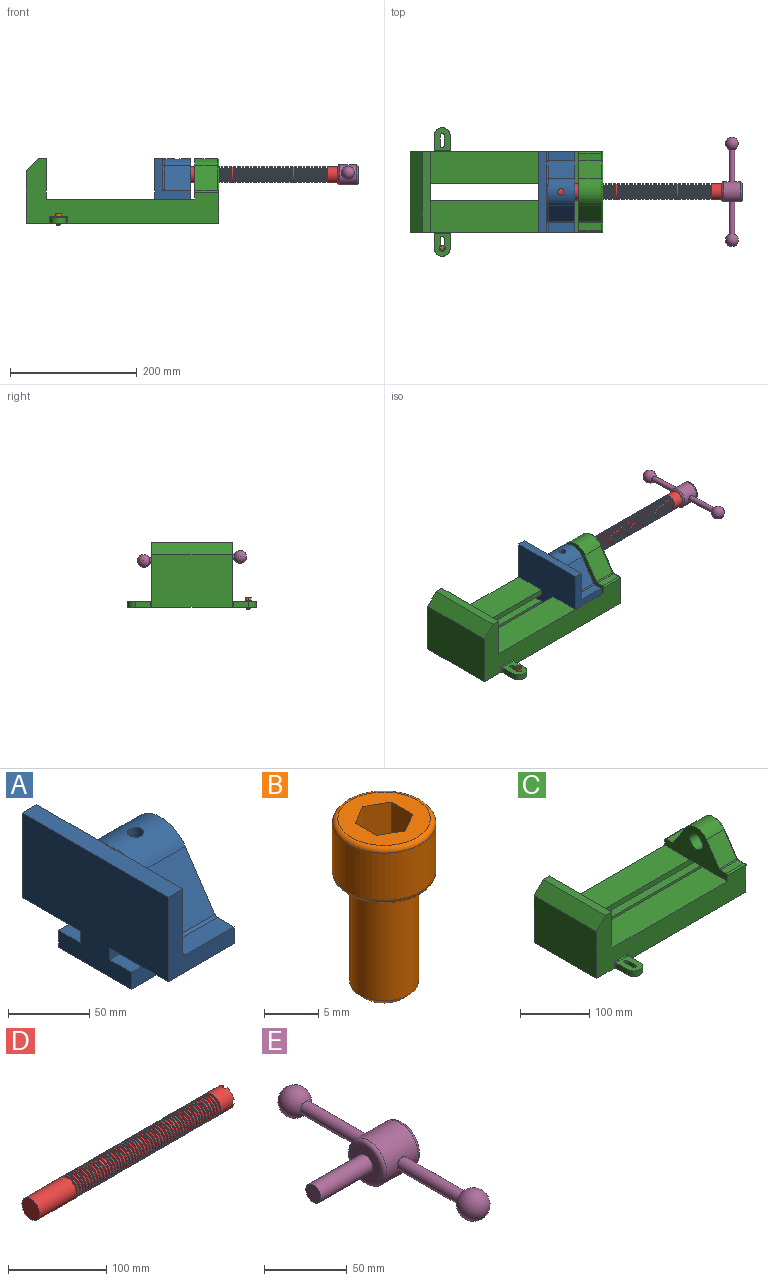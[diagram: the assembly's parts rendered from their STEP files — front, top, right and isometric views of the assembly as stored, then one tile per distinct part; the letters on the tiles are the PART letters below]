
ASSEMBLY  parts=5 mates=5
PART A: 36 faces, bbox 57.2x127x89 mm
  f0: plane 57.15x50.8mm, normal (0,0,-1), area 2903.2mm2, adj f6,f9,f10,f23
  f1: cylinder r=12.7mm len=44.45mm, axis (1,0,0), area 3464.3mm2, adj f6,f15,f16
  f2: plane 41.91x14.52mm, normal (0,0,1), area 608.5mm2, adj f6,f11,f24,f25
  f3: plane 51.86x48.26mm, normal (1,0,0), area 1495.7mm2, adj f8,f10,f31,f33,f35
  f4: plane 51.86x48.26mm, normal (1,0,0), area 1495.7mm2, adj f8,f11,f24,f28,f29
  f5: plane 57.15x50.8mm, normal (0,0,-1), area 2903.2mm2, adj f6,f9,f11,f22
  f6: plane 127x85.09mm, normal (1,0,0), area 5190.6mm2, adj f0,f1,f2,f5,f7,f10,f11,f12
  f7: plane 41.91x14.52mm, normal (0,0,1), area 608.5mm2, adj f6,f10,f30,f31
  f8: plane 127x12.7mm, normal (0,0,1), area 1612.9mm2, adj f3,f4,f9,f10,f11,f26,f34
  f9: plane 127x85.09mm, normal (-1,0,0), area 9096.8mm2, adj f0,f5,f8,f10,f11,f17,f18,f19
  f10: plane 63.5x57.15mm, normal (0,-1,0), area 1372.3mm2, adj f0,f3,f6,f7,f8,f9,f31
  f11: plane 63.5x57.15mm, normal (0,1,0), area 1372.3mm2, adj f2,f4,f5,f6,f8,f9,f24
  f12: plane 41.91x38.43mm, normal (0,-0.83,0.56), area 1939.2mm2, adj f6,f13,f30,f33
  f13: cylinder r=25.4mm len=44.45mm, axis (1,0,0), area 2026.5mm2, adj f6,f12,f14,f16,f26,f28,f34,f35
  f14: plane 41.91x38.43mm, normal (0,0.83,0.56), area 1939.2mm2, adj f6,f13,f25,f29
  f15: plane 25.4x25.4mm, normal (1,0,0), area 506.7mm2, adj f1
  f16: cylinder r=5.08mm len=13.76mm, axis (0,0,1), area 414mm2, adj f1,f13
  f17: plane 57.15x19.05mm, normal (0,0,1), area 1088.7mm2, adj f6,f9,f18,f23
  f18: plane 57.15x12.7mm, normal (0,-1,0), area 725.8mm2, adj f6,f9,f17,f19
  f19: plane 63.5x57.15mm, normal (0,0,-1), area 3629mm2, adj f6,f9,f18,f20
  f20: plane 57.15x12.7mm, normal (0,1,0), area 725.8mm2, adj f6,f9,f19,f21
  f21: plane 57.15x19.05mm, normal (0,0,1), area 1088.7mm2, adj f6,f9,f20,f22
  f22: plane 57.15x8.89mm, normal (0,1,0), area 508.1mm2, adj f5,f6,f9,f21
  f23: plane 57.15x8.89mm, normal (0,-1,0), area 508.1mm2, adj f0,f6,f9,f17
  f24: cylinder r=2.54mm len=14.52mm, axis (0,-1,0), area 57.9mm2, adj f2,f4,f11,f27
  f25: cylinder r=2.54mm len=41.91mm, axis (1,0,0), area 104.3mm2, adj f2,f6,f14,f27
  f26: bspline ~12.24x2.8mm, area 20.9mm2, adj f8,f13,f28
  f27: sphere r=2.54mm, area 6.3mm2, adj f24,f25,f29
  f28: torus R=27.94mm, axis (1,0,0), area 57.8mm2, adj f4,f13,f26,f29
  f29: cylinder r=2.54mm len=39.84mm, axis (0,-0.56,0.83), area 184.6mm2, adj f4,f14,f27,f28
  f30: cylinder r=2.54mm len=41.91mm, axis (1,0,0), area 104.3mm2, adj f6,f7,f12,f32
  f31: cylinder r=2.54mm len=14.52mm, axis (0,-1,0), area 57.9mm2, adj f3,f7,f10,f32
  f32: sphere r=2.54mm, area 6.3mm2, adj f30,f31,f33
  f33: cylinder r=2.54mm len=39.84mm, axis (0,-0.56,-0.83), area 184.6mm2, adj f3,f12,f32,f35
  f34: bspline ~12.24x2.8mm, area 20.9mm2, adj f8,f13,f35
  f35: torus R=27.94mm, axis (1,0,0), area 57.8mm2, adj f3,f13,f33,f34
PART B: 15 faces, bbox 10.3x10.3x19.1 mm
  f0: plane 8.51x8.51mm, normal (0,0,1), area 37.2mm2, adj f5,f6,f7,f8,f9,f10,f14
  f1: cylinder r=3.17mm len=11.94mm, axis (0,0,1), area 238.2mm2, adj f4,f12
  f2: plane 4.83x4.83mm, normal (0,0,-1), area 18.3mm2, adj f12
  f3: cylinder r=4.76mm len=9.53mm, axis (0,0,-1), area 159.6mm2, adj f13,f14
  f4: plane 8.51x8.51mm, normal (0,0,-1), area 25.2mm2, adj f1,f13
  f5: plane 4.83x2.38mm, normal (-0.5,-0.87,0), area 13.3mm2, adj f0,f6,f10,f11
  f6: plane 4.83x2.38mm, normal (0.5,-0.87,0), area 13.3mm2, adj f0,f5,f7,f11
  f7: plane 4.83x2.75mm, normal (1,0,0), area 13.3mm2, adj f0,f6,f8,f11
  f8: plane 4.83x2.38mm, normal (0.5,0.87,0), area 13.3mm2, adj f0,f7,f9,f11
  f9: plane 4.83x2.38mm, normal (-0.5,0.87,0), area 13.3mm2, adj f0,f8,f10,f11
  f10: plane 4.83x2.75mm, normal (-1,0,0), area 13.3mm2, adj f0,f5,f9,f11
  f11: plane 5.5x4.76mm, normal (0,0,1), area 19.6mm2, adj f5,f6,f7,f8,f9,f10
  f12: cone r=3.17mm half-angle=45deg, axis (0,0,1), area 18.9mm2, adj f1,f2
  f13: torus R=4.25mm, axis (0,0,1), area 23mm2, adj f3,f4
  f14: torus R=4.25mm, axis (0,0,1), area 23mm2, adj f0,f3
PART C: 61 faces, bbox 304.8x203.2x103.7 mm
  f0: plane 304.8x101.6mm, normal (0,1,0), area 13520.3mm2, adj f3,f4,f5,f6,f7,f8,f9,f16
  f1: plane 304.8x101.6mm, normal (0,-1,0), area 13520.3mm2, adj f2,f3,f5,f6,f7,f8,f9,f16
  f2: plane 234.95x50.8mm, normal (0,0,1), area 11935.5mm2, adj f1,f5,f16,f26
  f3: plane 127x99.06mm, normal (1,0,0), area 7097.5mm2, adj f0,f1,f9,f14,f17,f18,f19,f20
  f4: plane 234.95x50.8mm, normal (0,0,1), area 11935.5mm2, adj f0,f5,f16,f27
  f5: plane 127x101.6mm, normal (1,0,0), area 9516.1mm2, adj f0,f1,f2,f4,f6,f9,f18,f19
  f6: plane 127x12.7mm, normal (0,0,1), area 1612.9mm2, adj f0,f1,f5,f7
  f7: plane 127x19.05mm, normal (-0.71,0,0.71), area 3421.5mm2, adj f0,f1,f6,f8
  f8: plane 127x82.55mm, normal (-1,0,0), area 10483.8mm2, adj f0,f1,f7,f9
  f9: plane 304.8x203.2mm, normal (0,0,-1), area 33298.3mm2, adj f0,f1,f3,f5,f8,f21,f22,f39
  f10: plane 35.56x11.98mm, normal (0,0,1), area 426mm2, adj f16,f28,f29,f30
  f11: plane 38.43x35.56mm, normal (0,0.83,0.56), area 1645.4mm2, adj f12,f16,f29,f32
  f12: cylinder r=25.4mm len=42.19mm, axis (1,0,0), area 1770.2mm2, adj f11,f13,f16,f33
  f13: plane 38.43x35.56mm, normal (0,-0.83,0.56), area 1645.4mm2, adj f12,f16,f34,f35
  f14: cylinder r=12.7mm len=38.1mm, axis (1,0,0), area 3040.2mm2, adj f3,f16
  f15: plane 35.56x11.98mm, normal (0,0,1), area 426mm2, adj f16,f34,f36,f38
  f16: plane 127x63.5mm, normal (-1,0,0), area 4155.5mm2, adj f0,f1,f2,f4,f10,f11,f12,f13
  f17: plane 38.1x25.4mm, normal (0,0,-1), area 967.7mm2, adj f3,f16,f26,f27
  f18: plane 273.05x19.05mm, normal (0,0,-1), area 5201.6mm2, adj f3,f5,f19,f26
  f19: plane 273.05x12.7mm, normal (0,1,0), area 3467.7mm2, adj f3,f5,f18,f20
  f20: plane 273.05x19.05mm, normal (0,0,1), area 5201.6mm2, adj f3,f5,f19,f21
  f21: plane 273.05x16.51mm, normal (0,1,0), area 4508.1mm2, adj f3,f5,f9,f20
  f22: plane 273.05x16.51mm, normal (0,-1,0), area 4508.1mm2, adj f3,f5,f9,f23
  f23: plane 273.05x19.05mm, normal (0,0,1), area 5201.6mm2, adj f3,f5,f22,f24
  f24: plane 273.05x12.7mm, normal (0,-1,0), area 3467.7mm2, adj f3,f5,f23,f25
  f25: plane 273.05x19.05mm, normal (0,0,-1), area 5201.6mm2, adj f3,f5,f24,f27
  f26: plane 273.05x8.89mm, normal (0,1,0), area 2427.4mm2, adj f2,f3,f5,f17,f18
  f27: plane 273.05x8.89mm, normal (0,-1,0), area 2427.4mm2, adj f3,f4,f5,f17,f25
  f28: cylinder r=2.54mm len=38.1mm, axis (1,0,0), area 148.3mm2, adj f0,f10,f16,f30
  f29: cylinder r=2.54mm len=35.56mm, axis (-1,0,0), area 88.5mm2, adj f10,f11,f16,f31
  f30: cylinder r=2.54mm len=14.52mm, axis (0,1,0), area 54.3mm2, adj f3,f10,f28,f31
  f31: torus R=5.08mm, axis (-1,0,0), area 13.5mm2, adj f3,f29,f30,f32
  f32: cylinder r=2.54mm len=39.84mm, axis (0,0.56,-0.83), area 184.6mm2, adj f3,f11,f31,f33
  f33: torus R=22.86mm, axis (-1,0,0), area 191.4mm2, adj f3,f12,f32,f35
  f34: cylinder r=2.54mm len=35.56mm, axis (-1,0,0), area 88.5mm2, adj f13,f15,f16,f37
  f35: cylinder r=2.54mm len=39.84mm, axis (0,0.56,0.83), area 184.6mm2, adj f3,f13,f33,f37
  f36: cylinder r=2.54mm len=38.1mm, axis (-1,0,0), area 148.3mm2, adj f1,f15,f16,f38
  f37: torus R=5.08mm, axis (-1,0,0), area 13.5mm2, adj f3,f34,f35,f38
  f38: cylinder r=2.54mm len=14.52mm, axis (0,1,0), area 54.3mm2, adj f3,f15,f36,f37
  f39: plane 23.88x9.53mm, normal (-1,0,0), area 227.4mm2, adj f9,f45,f46,f60
  f40: plane 23.88x9.53mm, normal (1,0,0), area 227.4mm2, adj f9,f45,f46,f58
  f41: cylinder r=3.3mm len=9.53mm, axis (0,0,-1), area 98.8mm2, adj f9,f42,f44,f46
  f42: plane 15.62x9.53mm, normal (-1,0,0), area 148.8mm2, adj f9,f41,f43,f46
  f43: cylinder r=3.3mm len=9.53mm, axis (0,0,-1), area 98.8mm2, adj f9,f42,f44,f46
  f44: plane 15.62x9.53mm, normal (1,0,0), area 148.8mm2, adj f9,f41,f43,f46
  f45: cylinder r=12.7mm len=25.4mm, axis (0,0,-1), area 380mm2, adj f9,f39,f40,f46
  f46: plane 36.58x25.4mm, normal (0,0,1), area 722.4mm2, adj f39,f40,f41,f42,f43,f44,f45,f59
  f47: plane 23.88x9.53mm, normal (-1,0,0), area 227.4mm2, adj f9,f53,f54,f56
  f48: plane 23.88x9.53mm, normal (1,0,0), area 227.4mm2, adj f9,f53,f54,f55
  f49: cylinder r=3.3mm len=9.53mm, axis (0,0,-1), area 98.8mm2, adj f9,f50,f52,f54
  f50: plane 15.62x9.53mm, normal (-1,0,0), area 148.8mm2, adj f9,f49,f51,f54
  f51: cylinder r=3.3mm len=9.53mm, axis (0,0,-1), area 98.8mm2, adj f9,f50,f52,f54
  f52: plane 15.62x9.53mm, normal (1,0,0), area 148.8mm2, adj f9,f49,f51,f54
  f53: cylinder r=12.7mm len=25.4mm, axis (0,0,-1), area 380mm2, adj f9,f47,f48,f54
  f54: plane 36.58x25.4mm, normal (0,0,1), area 722.4mm2, adj f47,f48,f49,f50,f51,f52,f53,f57
  f55: cylinder r=1.52mm len=11.05mm, axis (0,0,-1), area 24.1mm2, adj f0,f9,f48,f57
  f56: cylinder r=1.52mm len=11.05mm, axis (0,0,1), area 24.1mm2, adj f0,f9,f47,f57
  f57: cylinder r=1.52mm len=28.45mm, axis (1,0,0), area 63.5mm2, adj f0,f54,f55,f56
  f58: cylinder r=1.52mm len=11.05mm, axis (0,0,1), area 24.1mm2, adj f1,f9,f40,f59
  f59: cylinder r=1.52mm len=28.45mm, axis (-1,0,0), area 63.5mm2, adj f1,f46,f58,f60
  f60: cylinder r=1.52mm len=11.05mm, axis (0,0,-1), area 24.1mm2, adj f1,f9,f39,f59
PART D: 220 faces, bbox 279.4x25.4x25.4 mm
  f0: cylinder r=12.7mm len=25.4mm, axis (-1,0,0), area 1468.2mm2, adj f1,f2,f3,f5,f7,f208,f209,f210
  f1: plane 9.9x9.9mm, normal (1,0,0), area 62.3mm2, adj f0,f4,f213,f216
  f2: plane 9.9x9.9mm, normal (1,0,0), area 62.3mm2, adj f0,f4,f210,f218
  f3: plane 9.9x9.9mm, normal (1,0,0), area 62.3mm2, adj f0,f4,f209,f212
  f4: cylinder r=6.35mm len=25.4mm, axis (1,0,0), area 960.3mm2, adj f1,f2,f3,f5,f6,f208,f209,f210
  f5: plane 9.9x9.9mm, normal (1,0,0), area 62.3mm2, adj f0,f4,f215,f217
  f6: plane 12.7x12.7mm, normal (1,0,0), area 126.7mm2, adj f4
  f7: cone r=12.7mm half-angle=76deg, axis (1,0,0), area 188mm2, adj f0,f9
  f8: cone r=10.16mm half-angle=76deg, axis (-1,0,0), area 188mm2, adj f9,f10
  f9: cylinder r=10.16mm len=20.32mm, axis (1,0,0), area 81.1mm2, adj f7,f8
  f10: cylinder r=12.7mm len=25.4mm, axis (-1,0,0), area 131.7mm2, adj f8,f11
  f11: cone r=12.7mm half-angle=76deg, axis (1,0,0), area 188mm2, adj f10,f13
  f12: cone r=10.16mm half-angle=76deg, axis (-1,0,0), area 188mm2, adj f13,f14
  f13: cylinder r=10.16mm len=20.32mm, axis (1,0,0), area 81.1mm2, adj f11,f12
  f14: cylinder r=12.7mm len=25.4mm, axis (-1,0,0), area 131.7mm2, adj f12,f15
  f15: cone r=12.7mm half-angle=76deg, axis (1,0,0), area 188mm2, adj f14,f17
  f16: cone r=10.16mm half-angle=76deg, axis (-1,0,0), area 188mm2, adj f17,f18
  f17: cylinder r=10.16mm len=20.32mm, axis (1,0,0), area 81.1mm2, adj f15,f16
  f18: cylinder r=12.7mm len=25.4mm, axis (-1,0,0), area 131.7mm2, adj f16,f19
  f19: cone r=12.7mm half-angle=76deg, axis (1,0,0), area 188mm2, adj f18,f21
  f20: cone r=10.16mm half-angle=76deg, axis (-1,0,0), area 188mm2, adj f21,f22
  f21: cylinder r=10.16mm len=20.32mm, axis (1,0,0), area 81.1mm2, adj f19,f20
  f22: cylinder r=12.7mm len=25.4mm, axis (-1,0,0), area 131.7mm2, adj f20,f23
  f23: cone r=12.7mm half-angle=76deg, axis (1,0,0), area 188mm2, adj f22,f25
  f24: cone r=10.16mm half-angle=76deg, axis (-1,0,0), area 188mm2, adj f25,f26
  f25: cylinder r=10.16mm len=20.32mm, axis (1,0,0), area 81.1mm2, adj f23,f24
  f26: cylinder r=12.7mm len=25.4mm, axis (-1,0,0), area 131.7mm2, adj f24,f27
  f27: cone r=12.7mm half-angle=76deg, axis (1,0,0), area 188mm2, adj f26,f29
  f28: cone r=10.16mm half-angle=76deg, axis (-1,0,0), area 188mm2, adj f29,f30
  f29: cylinder r=10.16mm len=20.32mm, axis (1,0,0), area 81.1mm2, adj f27,f28
  f30: cylinder r=12.7mm len=25.4mm, axis (-1,0,0), area 131.7mm2, adj f28,f31
  f31: cone r=12.7mm half-angle=76deg, axis (1,0,0), area 188mm2, adj f30,f33
  f32: cone r=10.16mm half-angle=76deg, axis (-1,0,0), area 188mm2, adj f33,f34
  f33: cylinder r=10.16mm len=20.32mm, axis (1,0,0), area 81.1mm2, adj f31,f32
  f34: cylinder r=12.7mm len=25.4mm, axis (-1,0,0), area 131.7mm2, adj f32,f35
  f35: cone r=12.7mm half-angle=76deg, axis (1,0,0), area 188mm2, adj f34,f37
  f36: cone r=10.16mm half-angle=76deg, axis (-1,0,0), area 188mm2, adj f37,f38
  f37: cylinder r=10.16mm len=20.32mm, axis (1,0,0), area 81.1mm2, adj f35,f36
  f38: cylinder r=12.7mm len=25.4mm, axis (-1,0,0), area 131.7mm2, adj f36,f39
  f39: cone r=12.7mm half-angle=76deg, axis (1,0,0), area 188mm2, adj f38,f41
  f40: cone r=10.16mm half-angle=76deg, axis (-1,0,0), area 188mm2, adj f41,f42
  f41: cylinder r=10.16mm len=20.32mm, axis (1,0,0), area 81.1mm2, adj f39,f40
  f42: cylinder r=12.7mm len=25.4mm, axis (-1,0,0), area 131.7mm2, adj f40,f43
  f43: cone r=12.7mm half-angle=76deg, axis (1,0,0), area 188mm2, adj f42,f45
  f44: cone r=10.16mm half-angle=76deg, axis (-1,0,0), area 188mm2, adj f45,f46
  f45: cylinder r=10.16mm len=20.32mm, axis (1,0,0), area 81.1mm2, adj f43,f44
  f46: cylinder r=12.7mm len=25.4mm, axis (-1,0,0), area 131.7mm2, adj f44,f47
  f47: cone r=12.7mm half-angle=76deg, axis (1,0,0), area 188mm2, adj f46,f49
  f48: cone r=10.16mm half-angle=76deg, axis (-1,0,0), area 188mm2, adj f49,f50
  f49: cylinder r=10.16mm len=20.32mm, axis (1,0,0), area 81.1mm2, adj f47,f48
  f50: cylinder r=12.7mm len=25.4mm, axis (-1,0,0), area 131.7mm2, adj f48,f51
  f51: cone r=12.7mm half-angle=76deg, axis (1,0,0), area 188mm2, adj f50,f53
  f52: cone r=10.16mm half-angle=76deg, axis (-1,0,0), area 188mm2, adj f53,f54
  f53: cylinder r=10.16mm len=20.32mm, axis (1,0,0), area 81.1mm2, adj f51,f52
  f54: cylinder r=12.7mm len=25.4mm, axis (-1,0,0), area 131.7mm2, adj f52,f55
  f55: cone r=12.7mm half-angle=76deg, axis (1,0,0), area 188mm2, adj f54,f57
  f56: cone r=10.16mm half-angle=76deg, axis (-1,0,0), area 188mm2, adj f57,f58
  f57: cylinder r=10.16mm len=20.32mm, axis (1,0,0), area 81.1mm2, adj f55,f56
  f58: cylinder r=12.7mm len=25.4mm, axis (-1,0,0), area 131.7mm2, adj f56,f59
  f59: cone r=12.7mm half-angle=76deg, axis (1,0,0), area 188mm2, adj f58,f61
  f60: cone r=10.16mm half-angle=76deg, axis (-1,0,0), area 188mm2, adj f61,f62
  f61: cylinder r=10.16mm len=20.32mm, axis (1,0,0), area 81.1mm2, adj f59,f60
  f62: cylinder r=12.7mm len=25.4mm, axis (-1,0,0), area 131.7mm2, adj f60,f63
  f63: cone r=12.7mm half-angle=76deg, axis (1,0,0), area 188mm2, adj f62,f65
  f64: cone r=10.16mm half-angle=76deg, axis (-1,0,0), area 188mm2, adj f65,f66
  f65: cylinder r=10.16mm len=20.32mm, axis (1,0,0), area 81.1mm2, adj f63,f64
  f66: cylinder r=12.7mm len=25.4mm, axis (-1,0,0), area 131.7mm2, adj f64,f67
  f67: cone r=12.7mm half-angle=76deg, axis (1,0,0), area 188mm2, adj f66,f69
  f68: cone r=10.16mm half-angle=76deg, axis (-1,0,0), area 188mm2, adj f69,f70
  f69: cylinder r=10.16mm len=20.32mm, axis (1,0,0), area 81.1mm2, adj f67,f68
  f70: cylinder r=12.7mm len=25.4mm, axis (-1,0,0), area 131.7mm2, adj f68,f71
  f71: cone r=12.7mm half-angle=76deg, axis (1,0,0), area 188mm2, adj f70,f73
  f72: cone r=10.16mm half-angle=76deg, axis (-1,0,0), area 188mm2, adj f73,f74
  f73: cylinder r=10.16mm len=20.32mm, axis (1,0,0), area 81.1mm2, adj f71,f72
  f74: cylinder r=12.7mm len=25.4mm, axis (-1,0,0), area 131.7mm2, adj f72,f75
  f75: cone r=12.7mm half-angle=76deg, axis (1,0,0), area 188mm2, adj f74,f77
  f76: cone r=10.16mm half-angle=76deg, axis (-1,0,0), area 188mm2, adj f77,f78
  f77: cylinder r=10.16mm len=20.32mm, axis (1,0,0), area 81.1mm2, adj f75,f76
  f78: cylinder r=12.7mm len=25.4mm, axis (-1,0,0), area 131.7mm2, adj f76,f79
  f79: cone r=12.7mm half-angle=76deg, axis (1,0,0), area 188mm2, adj f78,f81
  f80: cone r=10.16mm half-angle=76deg, axis (-1,0,0), area 188mm2, adj f81,f82
  f81: cylinder r=10.16mm len=20.32mm, axis (1,0,0), area 81.1mm2, adj f79,f80
  f82: cylinder r=12.7mm len=25.4mm, axis (-1,0,0), area 131.7mm2, adj f80,f83
  f83: cone r=12.7mm half-angle=76deg, axis (1,0,0), area 188mm2, adj f82,f85
  f84: cone r=10.16mm half-angle=76deg, axis (-1,0,0), area 188mm2, adj f85,f86
  f85: cylinder r=10.16mm len=20.32mm, axis (1,0,0), area 81.1mm2, adj f83,f84
  f86: cylinder r=12.7mm len=25.4mm, axis (-1,0,0), area 131.7mm2, adj f84,f87
  f87: cone r=12.7mm half-angle=76deg, axis (1,0,0), area 188mm2, adj f86,f89
  f88: cone r=10.16mm half-angle=76deg, axis (-1,0,0), area 188mm2, adj f89,f90
  f89: cylinder r=10.16mm len=20.32mm, axis (1,0,0), area 81.1mm2, adj f87,f88
  f90: cylinder r=12.7mm len=25.4mm, axis (-1,0,0), area 131.7mm2, adj f88,f91
  f91: cone r=12.7mm half-angle=76deg, axis (1,0,0), area 188mm2, adj f90,f93
  f92: cone r=10.16mm half-angle=76deg, axis (-1,0,0), area 188mm2, adj f93,f94
  f93: cylinder r=10.16mm len=20.32mm, axis (1,0,0), area 81.1mm2, adj f91,f92
  f94: cylinder r=12.7mm len=25.4mm, axis (-1,0,0), area 131.7mm2, adj f92,f95
  f95: cone r=12.7mm half-angle=76deg, axis (1,0,0), area 188mm2, adj f94,f97
  f96: cone r=10.16mm half-angle=76deg, axis (-1,0,0), area 188mm2, adj f97,f98
  f97: cylinder r=10.16mm len=20.32mm, axis (1,0,0), area 81.1mm2, adj f95,f96
  f98: cylinder r=12.7mm len=25.4mm, axis (-1,0,0), area 131.7mm2, adj f96,f99
  f99: cone r=12.7mm half-angle=76deg, axis (1,0,0), area 188mm2, adj f98,f101
  f100: cone r=10.16mm half-angle=76deg, axis (-1,0,0), area 188mm2, adj f101,f102
  f101: cylinder r=10.16mm len=20.32mm, axis (1,0,0), area 81.1mm2, adj f99,f100
  f102: cylinder r=12.7mm len=25.4mm, axis (-1,0,0), area 131.7mm2, adj f100,f103
  f103: cone r=12.7mm half-angle=76deg, axis (1,0,0), area 188mm2, adj f102,f105
  f104: cone r=10.16mm half-angle=76deg, axis (-1,0,0), area 188mm2, adj f105,f106
  f105: cylinder r=10.16mm len=20.32mm, axis (1,0,0), area 81.1mm2, adj f103,f104
  f106: cylinder r=12.7mm len=25.4mm, axis (-1,0,0), area 131.7mm2, adj f104,f107
  f107: cone r=12.7mm half-angle=76deg, axis (1,0,0), area 188mm2, adj f106,f109
  f108: cone r=10.16mm half-angle=76deg, axis (-1,0,0), area 188mm2, adj f109,f110
  f109: cylinder r=10.16mm len=20.32mm, axis (1,0,0), area 81.1mm2, adj f107,f108
  f110: cylinder r=12.7mm len=25.4mm, axis (-1,0,0), area 131.7mm2, adj f108,f111
  f111: cone r=12.7mm half-angle=76deg, axis (1,0,0), area 188mm2, adj f110,f113
  f112: cone r=10.16mm half-angle=76deg, axis (-1,0,0), area 188mm2, adj f113,f114
  f113: cylinder r=10.16mm len=20.32mm, axis (1,0,0), area 81.1mm2, adj f111,f112
  f114: cylinder r=12.7mm len=25.4mm, axis (-1,0,0), area 131.7mm2, adj f112,f115
  f115: cone r=12.7mm half-angle=76deg, axis (1,0,0), area 188mm2, adj f114,f117
  f116: cone r=10.16mm half-angle=76deg, axis (-1,0,0), area 188mm2, adj f117,f118
  f117: cylinder r=10.16mm len=20.32mm, axis (1,0,0), area 81.1mm2, adj f115,f116
  f118: cylinder r=12.7mm len=25.4mm, axis (-1,0,0), area 131.7mm2, adj f116,f119
  f119: cone r=12.7mm half-angle=76deg, axis (1,0,0), area 188mm2, adj f118,f121
  f120: cone r=10.16mm half-angle=76deg, axis (-1,0,0), area 188mm2, adj f121,f122
  f121: cylinder r=10.16mm len=20.32mm, axis (1,0,0), area 81.1mm2, adj f119,f120
  f122: cylinder r=12.7mm len=25.4mm, axis (-1,0,0), area 131.7mm2, adj f120,f123
  f123: cone r=12.7mm half-angle=76deg, axis (1,0,0), area 188mm2, adj f122,f125
  f124: cone r=10.16mm half-angle=76deg, axis (-1,0,0), area 188mm2, adj f125,f126
  f125: cylinder r=10.16mm len=20.32mm, axis (1,0,0), area 81.1mm2, adj f123,f124
  f126: cylinder r=12.7mm len=25.4mm, axis (-1,0,0), area 131.7mm2, adj f124,f127
  f127: cone r=12.7mm half-angle=76deg, axis (1,0,0), area 188mm2, adj f126,f129
  f128: cone r=10.16mm half-angle=76deg, axis (-1,0,0), area 188mm2, adj f129,f130
  f129: cylinder r=10.16mm len=20.32mm, axis (1,0,0), area 81.1mm2, adj f127,f128
  f130: cylinder r=12.7mm len=25.4mm, axis (-1,0,0), area 131.7mm2, adj f128,f131
  f131: cone r=12.7mm half-angle=76deg, axis (1,0,0), area 188mm2, adj f130,f133
  f132: cone r=10.16mm half-angle=76deg, axis (-1,0,0), area 188mm2, adj f133,f134
  f133: cylinder r=10.16mm len=20.32mm, axis (1,0,0), area 81.1mm2, adj f131,f132
  f134: cylinder r=12.7mm len=25.4mm, axis (-1,0,0), area 131.7mm2, adj f132,f135
  f135: cone r=12.7mm half-angle=76deg, axis (1,0,0), area 188mm2, adj f134,f137
  f136: cone r=10.16mm half-angle=76deg, axis (-1,0,0), area 188mm2, adj f137,f138
  f137: cylinder r=10.16mm len=20.32mm, axis (1,0,0), area 81.1mm2, adj f135,f136
  f138: cylinder r=12.7mm len=25.4mm, axis (-1,0,0), area 131.7mm2, adj f136,f139
  f139: cone r=12.7mm half-angle=76deg, axis (1,0,0), area 188mm2, adj f138,f141
  f140: cone r=10.16mm half-angle=76deg, axis (-1,0,0), area 188mm2, adj f141,f142
  f141: cylinder r=10.16mm len=20.32mm, axis (1,0,0), area 81.1mm2, adj f139,f140
  f142: cylinder r=12.7mm len=25.4mm, axis (-1,0,0), area 131.7mm2, adj f140,f143
  f143: cone r=12.7mm half-angle=76deg, axis (1,0,0), area 188mm2, adj f142,f145
  f144: cone r=10.16mm half-angle=76deg, axis (-1,0,0), area 188mm2, adj f145,f146
  f145: cylinder r=10.16mm len=20.32mm, axis (1,0,0), area 81.1mm2, adj f143,f144
  f146: cylinder r=12.7mm len=25.4mm, axis (-1,0,0), area 131.7mm2, adj f144,f147
  f147: cone r=12.7mm half-angle=76deg, axis (1,0,0), area 188mm2, adj f146,f149
  f148: cone r=10.16mm half-angle=76deg, axis (-1,0,0), area 188mm2, adj f149,f150
  f149: cylinder r=10.16mm len=20.32mm, axis (1,0,0), area 81.1mm2, adj f147,f148
  f150: cylinder r=12.7mm len=25.4mm, axis (-1,0,0), area 131.7mm2, adj f148,f151
  f151: cone r=12.7mm half-angle=76deg, axis (1,0,0), area 188mm2, adj f150,f153
  f152: cone r=10.16mm half-angle=76deg, axis (-1,0,0), area 188mm2, adj f153,f154
  f153: cylinder r=10.16mm len=20.32mm, axis (1,0,0), area 81.1mm2, adj f151,f152
  f154: cylinder r=12.7mm len=25.4mm, axis (-1,0,0), area 131.7mm2, adj f152,f155
  f155: cone r=12.7mm half-angle=76deg, axis (1,0,0), area 188mm2, adj f154,f157
  f156: cone r=10.16mm half-angle=76deg, axis (-1,0,0), area 188mm2, adj f157,f158
  f157: cylinder r=10.16mm len=20.32mm, axis (1,0,0), area 81.1mm2, adj f155,f156
  f158: cylinder r=12.7mm len=25.4mm, axis (-1,0,0), area 131.7mm2, adj f156,f159
  f159: cone r=12.7mm half-angle=76deg, axis (1,0,0), area 188mm2, adj f158,f161
  f160: cone r=10.16mm half-angle=76deg, axis (-1,0,0), area 188mm2, adj f161,f162
  f161: cylinder r=10.16mm len=20.32mm, axis (1,0,0), area 81.1mm2, adj f159,f160
  f162: cylinder r=12.7mm len=25.4mm, axis (-1,0,0), area 131.7mm2, adj f160,f163
  f163: cone r=12.7mm half-angle=76deg, axis (1,0,0), area 188mm2, adj f162,f165
  f164: cone r=10.16mm half-angle=76deg, axis (-1,0,0), area 188mm2, adj f165,f166
  f165: cylinder r=10.16mm len=20.32mm, axis (1,0,0), area 81.1mm2, adj f163,f164
  f166: cylinder r=12.7mm len=25.4mm, axis (-1,0,0), area 131.7mm2, adj f164,f167
  f167: cone r=12.7mm half-angle=76deg, axis (1,0,0), area 188mm2, adj f166,f169
  f168: cone r=10.16mm half-angle=76deg, axis (-1,0,0), area 188mm2, adj f169,f170
  f169: cylinder r=10.16mm len=20.32mm, axis (1,0,0), area 81.1mm2, adj f167,f168
  f170: cylinder r=12.7mm len=25.4mm, axis (-1,0,0), area 131.7mm2, adj f168,f171
  f171: cone r=12.7mm half-angle=76deg, axis (1,0,0), area 188mm2, adj f170,f173
  f172: cone r=10.16mm half-angle=76deg, axis (-1,0,0), area 188mm2, adj f173,f174
  f173: cylinder r=10.16mm len=20.32mm, axis (1,0,0), area 81.1mm2, adj f171,f172
  f174: cylinder r=12.7mm len=25.4mm, axis (-1,0,0), area 131.7mm2, adj f172,f175
  f175: cone r=12.7mm half-angle=76deg, axis (1,0,0), area 188mm2, adj f174,f177
  f176: cone r=10.16mm half-angle=76deg, axis (-1,0,0), area 188mm2, adj f177,f178
  f177: cylinder r=10.16mm len=20.32mm, axis (1,0,0), area 81.1mm2, adj f175,f176
  f178: cylinder r=12.7mm len=25.4mm, axis (-1,0,0), area 131.7mm2, adj f176,f179
  f179: cone r=12.7mm half-angle=76deg, axis (1,0,0), area 188mm2, adj f178,f181
  f180: cone r=10.16mm half-angle=76deg, axis (-1,0,0), area 188mm2, adj f181,f182
  f181: cylinder r=10.16mm len=20.32mm, axis (1,0,0), area 81.1mm2, adj f179,f180
  f182: cylinder r=12.7mm len=25.4mm, axis (-1,0,0), area 131.7mm2, adj f180,f183
  f183: cone r=12.7mm half-angle=76deg, axis (1,0,0), area 188mm2, adj f182,f185
  f184: cone r=10.16mm half-angle=76deg, axis (-1,0,0), area 188mm2, adj f185,f186
  f185: cylinder r=10.16mm len=20.32mm, axis (1,0,0), area 81.1mm2, adj f183,f184
  f186: cylinder r=12.7mm len=25.4mm, axis (-1,0,0), area 131.7mm2, adj f184,f187
  f187: cone r=12.7mm half-angle=76deg, axis (1,0,0), area 188mm2, adj f186,f189
  f188: cone r=10.16mm half-angle=76deg, axis (-1,0,0), area 188mm2, adj f189,f190
  f189: cylinder r=10.16mm len=20.32mm, axis (1,0,0), area 81.1mm2, adj f187,f188
  f190: cylinder r=12.7mm len=25.4mm, axis (-1,0,0), area 131.7mm2, adj f188,f191
  f191: cone r=12.7mm half-angle=76deg, axis (1,0,0), area 188mm2, adj f190,f193
  f192: cone r=10.16mm half-angle=76deg, axis (-1,0,0), area 188mm2, adj f193,f194
  f193: cylinder r=10.16mm len=20.32mm, axis (1,0,0), area 81.1mm2, adj f191,f192
  f194: cylinder r=12.7mm len=25.4mm, axis (-1,0,0), area 131.7mm2, adj f192,f195
  f195: cone r=12.7mm half-angle=76deg, axis (1,0,0), area 188mm2, adj f194,f197
  f196: cone r=10.16mm half-angle=76deg, axis (-1,0,0), area 188mm2, adj f197,f198
  f197: cylinder r=10.16mm len=20.32mm, axis (1,0,0), area 81.1mm2, adj f195,f196
  f198: cylinder r=12.7mm len=25.4mm, axis (-1,0,0), area 131.7mm2, adj f196,f199
  f199: cone r=12.7mm half-angle=76deg, axis (1,0,0), area 188mm2, adj f198,f201
  f200: cone r=10.16mm half-angle=76deg, axis (-1,0,0), area 188mm2, adj f201,f202
  f201: cylinder r=10.16mm len=20.32mm, axis (1,0,0), area 81.1mm2, adj f199,f200
  f202: cylinder r=12.7mm len=25.4mm, axis (-1,0,0), area 131.7mm2, adj f200,f203
  f203: cone r=12.7mm half-angle=76deg, axis (1,0,0), area 188mm2, adj f202,f205
  f204: cone r=10.16mm half-angle=76deg, axis (-1,0,0), area 188mm2, adj f205,f207
  f205: cylinder r=10.16mm len=20.32mm, axis (1,0,0), area 81.1mm2, adj f203,f204
  f206: plane 25.4x25.4mm, normal (-1,0,0), area 506.7mm2, adj f207
  f207: cylinder r=12.7mm len=52.45mm, axis (-1,0,0), area 4185.4mm2, adj f204,f206
  f208: plane 6.88x5.08mm, normal (1,0,0), area 32.7mm2, adj f0,f4,f209,f210
  f209: plane 6.62x2.54mm, normal (0,-1,0), area 16.8mm2, adj f0,f3,f4,f208
  f210: plane 6.62x2.54mm, normal (0,1,0), area 16.8mm2, adj f0,f2,f4,f208
  f211: plane 6.88x5.08mm, normal (1,0,0), area 32.7mm2, adj f0,f4,f212,f213
  f212: plane 6.62x2.54mm, normal (0,0,1), area 16.8mm2, adj f0,f3,f4,f211
  f213: plane 6.62x2.54mm, normal (0,0,-1), area 16.8mm2, adj f0,f1,f4,f211
  f214: plane 6.88x5.08mm, normal (1,0,0), area 32.7mm2, adj f0,f4,f215,f216
  f215: plane 6.62x2.54mm, normal (0,1,0), area 16.8mm2, adj f0,f4,f5,f214
  f216: plane 6.62x2.54mm, normal (0,-1,0), area 16.8mm2, adj f0,f1,f4,f214
  f217: plane 6.62x2.54mm, normal (0,0,-1), area 16.8mm2, adj f0,f4,f5,f219
  f218: plane 6.62x2.54mm, normal (0,0,1), area 16.8mm2, adj f0,f2,f4,f219
  f219: plane 6.88x5.08mm, normal (1,0,0), area 32.7mm2, adj f0,f4,f217,f218
PART E: 11 faces, bbox 76.2x172.7x34.4 mm
  f0: sphere r=10.16mm, area 1231.8mm2, adj f1
  f1: cylinder r=4.45mm len=51.82mm, axis (0,1,0), area 1438.5mm2, adj f0,f4
  f2: sphere r=10.16mm, area 1231.8mm2, adj f3
  f3: cylinder r=4.45mm len=51.82mm, axis (0,1,0), area 1438.5mm2, adj f2,f4
  f4: cylinder r=15.88mm len=31.75mm, axis (-1,0,0), area 2534.7mm2, adj f1,f3,f9,f10
  f5: cylinder r=6.35mm len=44.45mm, axis (-1,0,0), area 1773.5mm2, adj f6,f8
  f6: plane 12.7x12.7mm, normal (-1,0,0), area 126.7mm2, adj f5
  f7: plane 26.67x26.67mm, normal (1,0,0), area 558.6mm2, adj f10
  f8: plane 26.67x26.67mm, normal (-1,0,0), area 432mm2, adj f5,f9
  f9: torus R=13.33mm, axis (1,0,0), area 374.8mm2, adj f4,f8
  f10: torus R=13.33mm, axis (1,0,0), area 374.8mm2, adj f4,f7
PLACE A t=(171.54,0,0)mm
PLACE B rot(axis=(0,0,1),90deg) t=(-254,-88.9,9.52)mm
PLACE C at identity fixed
PLACE D rot(axis=(-1,0,0),2.4deg) t=(171.54,-3.25,0.07)mm
PLACE E rot(axis=(-1,0,0),2.4deg) t=(149.95,-3.25,0.07)mm
MATE fastened D.f4 <-> E.f5  axis (1,0,0) through (188.05,0,76.2)mm
MATE planar A.f0 <-> C.f2  axis (0,0,-1) through (-72.94,-38.1,38.1)mm
MATE pin_slot B.f1 <-> C.f41  axis (0,0,1) through (-254,-88.9,9.52)mm
MATE revolute D.f7 <-> A.f28  axis (-1,0,0) through (-88.81,0,76.2)mm
MATE cylindrical C.f12 <-> D.f7  axis (-1,0,0) through (-38.1,0,76.2)mm
